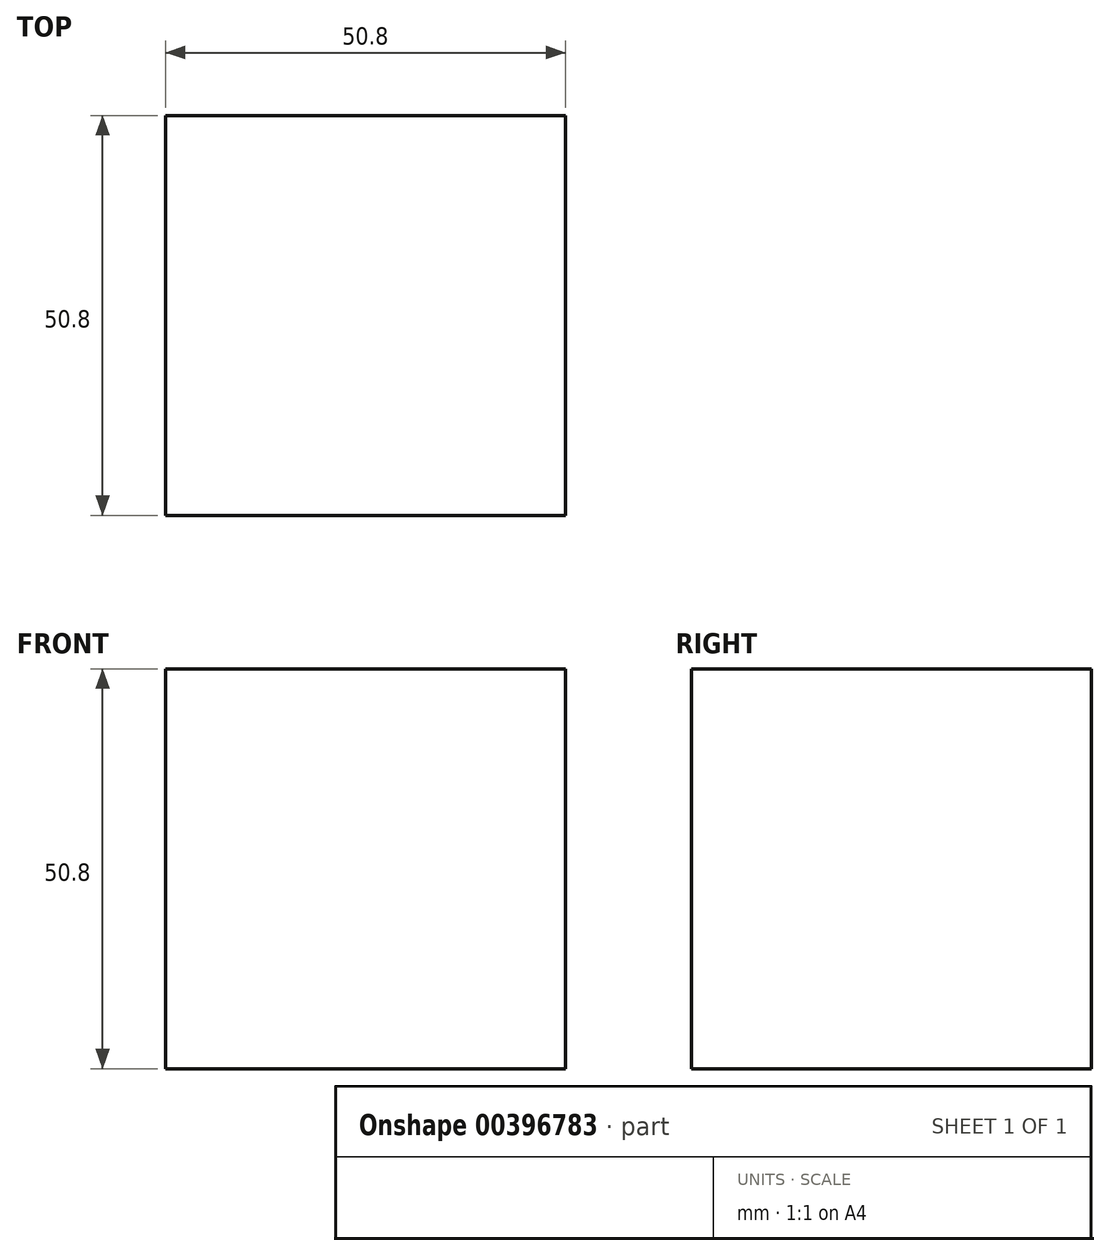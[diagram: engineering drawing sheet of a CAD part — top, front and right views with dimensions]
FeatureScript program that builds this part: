
annotation { "Feature Type Name" : "Feature", "Feature Type Description" : "" }
export const myFeature = defineFeature(function(context is Context, id is Id, definition is map)
    precondition{}
    {
        {
            var Q0;
            Q0=qCreatedBy(makeId("Front.planeOp"),FACE);
            var sketch = newSketch(context, id + "F0", { "sketchPlane" : qUnion([Q0])});
            skLineSegment(sketch, "E0.bottom", {"start": v(-50.8, 50.8) * mm, "end": v(0, 50.8) * mm});
            skLineSegment(sketch, "E0.top", {"start": v(-50.8, 0) * mm, "end": v(0, 0) * mm});
            skLineSegment(sketch, "E0.left", {"start": v(-50.8, 50.8) * mm, "end": v(-50.8, 0) * mm});
            skLineSegment(sketch, "E0.right", {"start": v(0, 50.8) * mm, "end": v(0, 0) * mm});
            skSolve(sketch);
        }
        {
            var Q0;
            Q0 = qSketchRegion(id + "F0", true);
            extrude(context, id + "F1", {"entities" : qUnion([Q0]), "depth" : 50.8 * mm});
        }
    });
